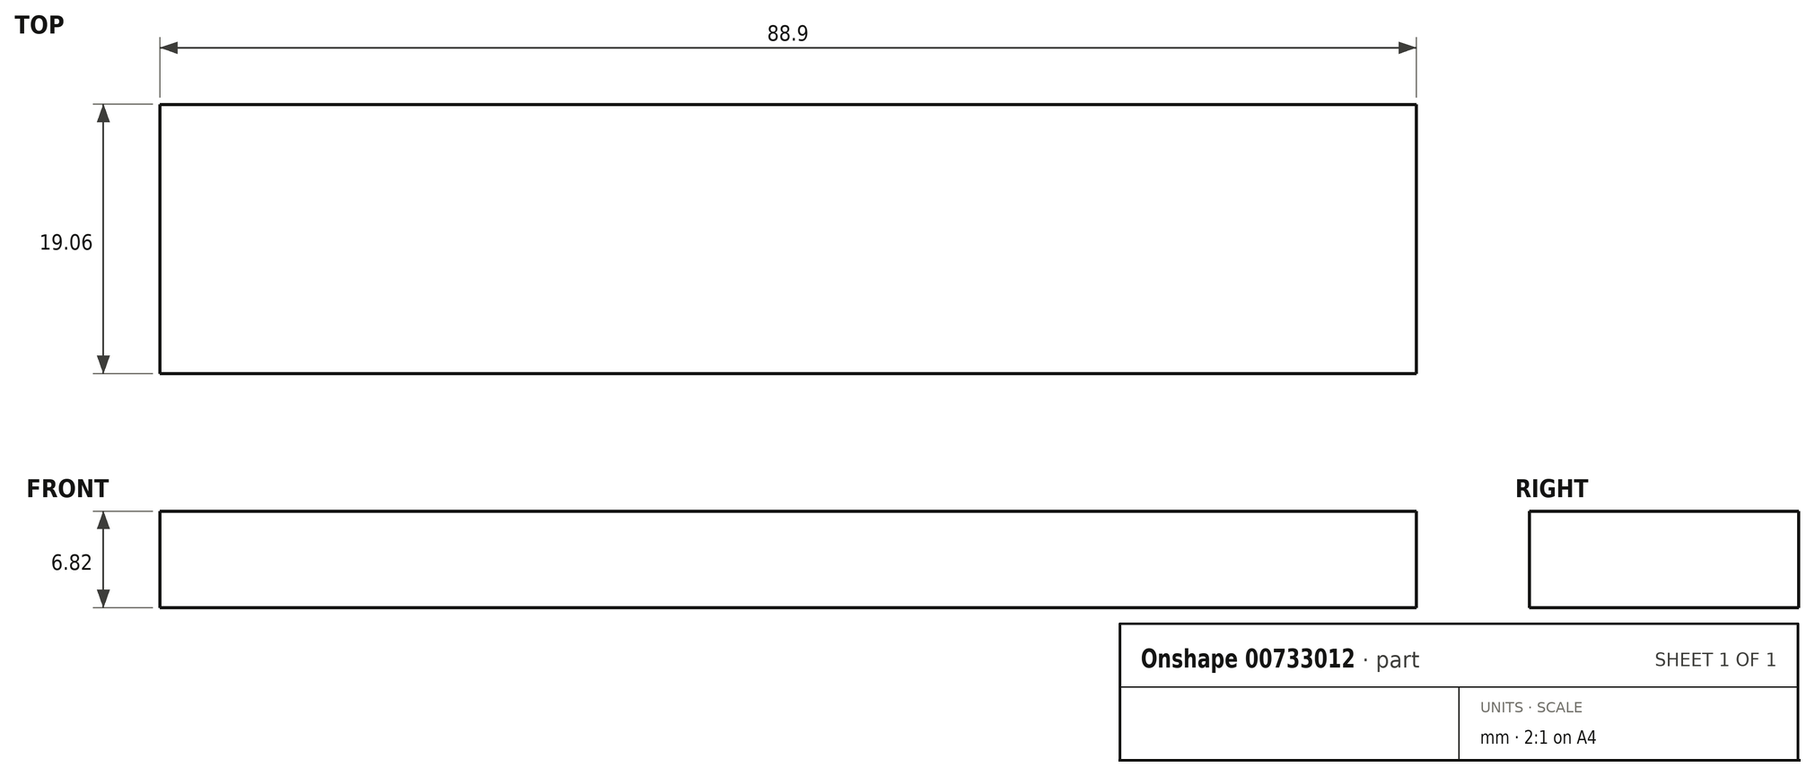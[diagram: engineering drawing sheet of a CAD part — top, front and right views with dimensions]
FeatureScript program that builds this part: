
annotation { "Feature Type Name" : "Feature", "Feature Type Description" : "" }
export const myFeature = defineFeature(function(context is Context, id is Id, definition is map)
    precondition{}
    {
        {
            var Q0;
            Q0=qCreatedBy(makeId("Front.planeOp"),FACE);
            var sketch = newSketch(context, id + "F0", { "sketchPlane" : qUnion([Q0])});
            skLineSegment(sketch, "E0.bottom", {"start": v(-19.75, 5.93) * mm, "end": v(69.15, 5.93) * mm});
            skLineSegment(sketch, "E0.top", {"start": v(-19.75, -0.9) * mm, "end": v(69.15, -0.9) * mm});
            skLineSegment(sketch, "E0.left", {"start": v(-19.75, 5.93) * mm, "end": v(-19.75, -0.9) * mm});
            skLineSegment(sketch, "E0.right", {"start": v(69.15, 5.93) * mm, "end": v(69.15, -0.9) * mm});
            skSolve(sketch);
        }
        {
            var Q0;
            Q0=makeQuery(id+"F0.imprint","IMPRINT",FACE,{"disambiguationData":[TD([[makeQuery(id+"F0.imprint","IMPRINT",EDGE,{"derivedFrom":sQuery(id+"F0.wireOp",EDGE,"E0.bottom")}),-1.0]])]});
            extrude(context, id + "F1", {"entities" : qUnion([Q0]), "endBound" : BoundingType.SYMMETRIC, "depth" : 19.05 * mm, "offsetDistance" : 25.4 * mm});
        }
    });
